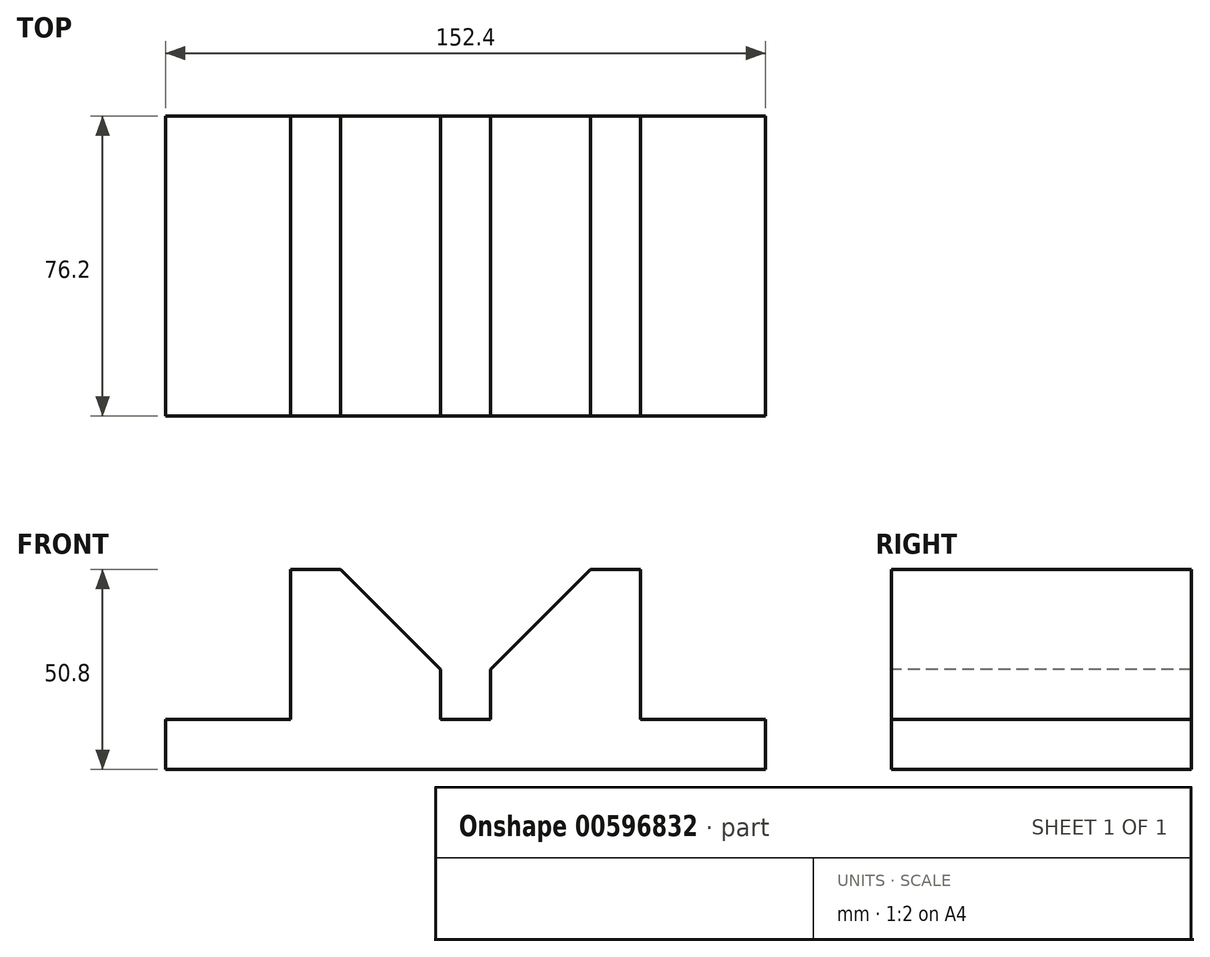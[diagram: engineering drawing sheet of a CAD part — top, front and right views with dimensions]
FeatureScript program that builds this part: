
annotation { "Feature Type Name" : "Feature", "Feature Type Description" : "" }
export const myFeature = defineFeature(function(context is Context, id is Id, definition is map)
    precondition{}
    {
        {
            var Q0;
            Q0=qCreatedBy(makeId("Front.planeOp"),FACE);
            var sketch = newSketch(context, id + "F0", { "sketchPlane" : qUnion([Q0])});
            skLineSegment(sketch, "E0.bottom", {"start": v(0, 0) * mm, "end": v(152.4, 0) * mm});
            skLineSegment(sketch, "E0.top", {"start": v(0, 50.8) * mm, "end": v(152.4, 50.8) * mm});
            skLineSegment(sketch, "E0.left", {"start": v(0, 0) * mm, "end": v(0, 50.8) * mm});
            skLineSegment(sketch, "E0.right", {"start": v(152.4, 0) * mm, "end": v(152.4, 50.8) * mm});
            skSolve(sketch);
        }
        {
            var Q0;
            Q0=makeQuery(id+"F0.imprint","IMPRINT",FACE,{"disambiguationData":[TD([[makeQuery(id+"F0.imprint","IMPRINT",EDGE,{"derivedFrom":sQuery(id+"F0.wireOp",EDGE,"E0.bottom")}),1.0]])]});
            extrude(context, id + "F1", {"entities" : qUnion([Q0]), "depth" : 76.2 * mm, "offsetDistance" : 25.4 * mm});
        }
        {
            var Q0;
            Q0=makeQuery(id+"F1.opExtrude","CAP_FACE",FACE,{"disambiguationData":[OSD([sQuery(id+"F0.wireOp",EDGE,"E0.bottom"),sQuery(id+"F0.wireOp",EDGE,"E0.top"),sQuery(id+"F0.wireOp",EDGE,"E0.left"),sQuery(id+"F0.wireOp",EDGE,"E0.right")])],"isStart":false});
            var sketch = newSketch(context, id + "F2", { "sketchPlane" : qUnion([Q0])});
            skLineSegment(sketch, "E1.0.0", {"start": v(152.4, 50.8) * mm, "end": v(0, 50.8) * mm});
            skLineSegment(sketch, "E1.0.1", {"start": v(0, 50.8) * mm, "end": v(0, 0) * mm});
            skLineSegment(sketch, "E1.0.2", {"start": v(0, 0) * mm, "end": v(152.4, 0) * mm});
            skLineSegment(sketch, "E1.0.3", {"start": v(152.4, 0) * mm, "end": v(152.4, 50.8) * mm});
            skLineSegment(sketch, "E2", {"start": v(0, 0) * mm, "end": v(0, 12.7) * mm});
            skLineSegment(sketch, "E3", {"start": v(0, 12.7) * mm, "end": v(31.75, 12.7) * mm});
            skLineSegment(sketch, "E4", {"start": v(31.75, 12.7) * mm, "end": v(31.75, 50.8) * mm});
            skLineSegment(sketch, "E5", {"start": v(31.75, 50.8) * mm, "end": v(44.45, 50.8) * mm});
            skLineSegment(sketch, "E6", {"start": v(152.4, 0) * mm, "end": v(152.4, 12.7) * mm});
            skLineSegment(sketch, "E7", {"start": v(152.4, 12.7) * mm, "end": v(120.65, 12.7) * mm});
            skLineSegment(sketch, "E8", {"start": v(120.65, 12.7) * mm, "end": v(120.65, 50.8) * mm});
            skLineSegment(sketch, "E9", {"start": v(120.65, 50.8) * mm, "end": v(107.95, 50.8) * mm});
            skLineSegment(sketch, "E10", {"start": v(76.2, 0) * mm, "end": v(82.55, 0) * mm});
            skLineSegment(sketch, "E11", {"start": v(82.55, 0) * mm, "end": v(69.85, 0) * mm});
            skLineSegment(sketch, "E12", {"start": v(69.85, 12.7) * mm, "end": v(82.55, 12.7) * mm});
            skLineSegment(sketch, "E13", {"start": v(69.85, 12.7) * mm, "end": v(69.85, 25.4) * mm});
            skLineSegment(sketch, "E14", {"start": v(82.55, 12.7) * mm, "end": v(82.55, 25.4) * mm});
            skLineSegment(sketch, "E15", {"start": v(44.45, 50.8) * mm, "end": v(69.85, 25.4) * mm});
            skLineSegment(sketch, "E16", {"start": v(82.55, 25.4) * mm, "end": v(107.95, 50.8) * mm});
            skSolve(sketch);
        }
        {
            var Q0;
            {var subQ0=sQuery(id+"F2.wireOp",EDGE,"E1.0.1");Q0=makeQuery(id+"F2.imprint","IMPRINT",FACE,{"disambiguationData":[TD([[makeQuery(id+"F2.imprint","IMPRINT",EDGE,{"derivedFrom":subQ0}),-1.0]])]});}
            var Q1;
            Q1=makeQuery(id+"F2.imprint","IMPRINT",FACE,{"disambiguationData":[TD([[makeQuery(id+"F2.imprint","IMPRINT",EDGE,{"derivedFrom":sQuery(id+"F2.wireOp",EDGE,"E12")}),1.0]])]});
            var Q2;
            {var subQ0=sQuery(id+"F2.wireOp",EDGE,"E1.0.3");Q2=makeQuery(id+"F2.imprint","IMPRINT",FACE,{"disambiguationData":[TD([[makeQuery(id+"F2.imprint","IMPRINT",EDGE,{"derivedFrom":subQ0}),1.0]])]});}
            extrude(context, id + "F3", {"entities" : qUnion([Q0, Q1, Q2]), "operationType" : NewBodyOperationType.REMOVE, "oppositeDirection" : true, "depth" : 76.2 * mm, "offsetDistance" : 25.4 * mm});
        }
    });
